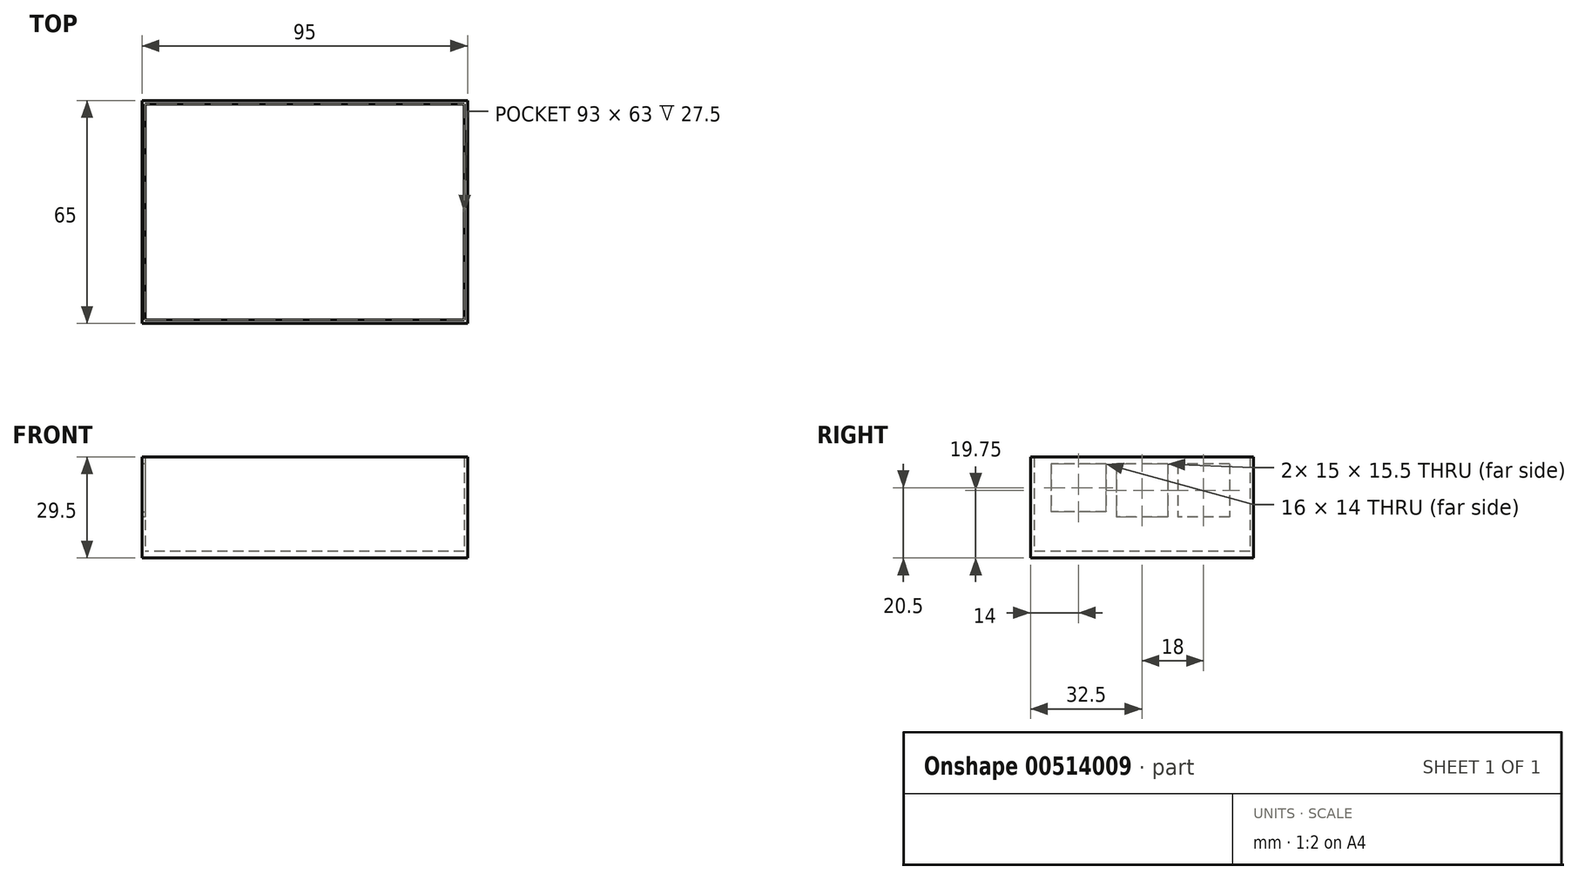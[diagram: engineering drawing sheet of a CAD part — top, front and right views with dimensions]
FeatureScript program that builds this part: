
annotation { "Feature Type Name" : "Feature", "Feature Type Description" : "" }
export const myFeature = defineFeature(function(context is Context, id is Id, definition is map)
    precondition{}
    {
        {
            var Q0;
            Q0=qCreatedBy(makeId("Top.planeOp"),FACE);
            var sketch = newSketch(context, id + "F0", { "sketchPlane" : qUnion([Q0])});
            skLineSegment(sketch, "E0.bottom", {"start": v(46.5, 31.5) * mm, "end": v(-46.5, 31.5) * mm});
            skLineSegment(sketch, "E0.top", {"start": v(46.5, -31.5) * mm, "end": v(-46.5, -31.5) * mm});
            skLineSegment(sketch, "E0.left", {"start": v(46.5, 31.5) * mm, "end": v(46.5, -31.5) * mm});
            skLineSegment(sketch, "E0.right", {"start": v(-46.5, 31.5) * mm, "end": v(-46.5, -31.5) * mm});
            skPoint(sketch, "E0.middle", {"position": v(0, 0) * mm});
            skLineSegment(sketch, "E1.bottom", {"start": v(47.5, 32.5) * mm, "end": v(-47.5, 32.5) * mm});
            skLineSegment(sketch, "E1.top", {"start": v(47.5, -32.5) * mm, "end": v(-47.5, -32.5) * mm});
            skLineSegment(sketch, "E1.left", {"start": v(47.5, 32.5) * mm, "end": v(47.5, -32.5) * mm});
            skLineSegment(sketch, "E1.right", {"start": v(-47.5, 32.5) * mm, "end": v(-47.5, -32.5) * mm});
            skSolve(sketch);
        }
        {
            var Q0;
            Q0=makeQuery(id+"F0.imprint","IMPRINT",FACE,{"disambiguationData":[TD([[makeQuery(id+"F0.imprint","IMPRINT",EDGE,{"derivedFrom":sQuery(id+"F0.wireOp",EDGE,"E0.bottom")}),-1.0]])]});
            extrude(context, id + "F1", {"entities" : qUnion([Q0]), "depth" : 12 * mm, "offsetDistance" : 25 * mm});
        }
        {
            var Q0;
            Q0=makeQuery(id+"F0.imprint","IMPRINT",FACE,{"disambiguationData":[TD([[makeQuery(id+"F0.imprint","IMPRINT",EDGE,{"derivedFrom":sQuery(id+"F0.wireOp",EDGE,"E0.bottom")}),1.0]])]});
            extrude(context, id + "F2", {"entities" : qUnion([Q0]), "operationType" : NewBodyOperationType.ADD, "depth" : 2 * mm, "offsetDistance" : 25 * mm});
        }
        {
            var Q0;
            Q0=makeQuery(id+"F1.opExtrude","CAP_FACE",FACE,{"disambiguationData":[OSD([sQuery(id+"F0.wireOp",EDGE,"E0.bottom"),sQuery(id+"F0.wireOp",EDGE,"E0.top"),sQuery(id+"F0.wireOp",EDGE,"E0.left"),sQuery(id+"F0.wireOp",EDGE,"E0.right"),sQuery(id+"F0.wireOp",EDGE,"E1.bottom"),sQuery(id+"F0.wireOp",EDGE,"E1.top"),sQuery(id+"F0.wireOp",EDGE,"E1.left"),sQuery(id+"F0.wireOp",EDGE,"E1.right")])],"isStart":false});
            var sketch = newSketch(context, id + "F3", { "sketchPlane" : qUnion([Q0])});
            skLineSegment(sketch, "E2.0", {"start": v(-47.5, 32.5) * mm, "end": v(-47.5, 25.5) * mm});
            skLineSegment(sketch, "E3.0", {"start": v(-46.5, 31.5) * mm, "end": v(-46.5, 25.5) * mm});
            skLineSegment(sketch, "E4.0", {"start": v(46.5, 31.5) * mm, "end": v(-46.5, 31.5) * mm});
            skLineSegment(sketch, "E5.0", {"start": v(47.5, 32.5) * mm, "end": v(-47.5, 32.5) * mm});
            skLineSegment(sketch, "E6.0", {"start": v(46.5, 31.5) * mm, "end": v(46.5, -31.5) * mm});
            skLineSegment(sketch, "E7.0", {"start": v(47.5, 32.5) * mm, "end": v(47.5, -32.5) * mm});
            skLineSegment(sketch, "E8.0", {"start": v(47.5, -32.5) * mm, "end": v(-47.5, -32.5) * mm});
            skLineSegment(sketch, "E9.0", {"start": v(46.5, -31.5) * mm, "end": v(-46.5, -31.5) * mm});
            skLineSegment(sketch, "E10", {"start": v(-46.5, 7.5) * mm, "end": v(-47.5, 7.5) * mm});
            skLineSegment(sketch, "E11", {"start": v(-46.5, -7.5) * mm, "end": v(-47.5, -7.5) * mm});
            skLineSegment(sketch, "E12", {"start": v(-46.5, 10.5) * mm, "end": v(-47.5, 10.5) * mm});
            skLineSegment(sketch, "E13", {"start": v(-47.5, 25.5) * mm, "end": v(-46.5, 25.5) * mm});
            skLineSegment(sketch, "E14.trimOffspring", {"start": v(-46.5, -7.5) * mm, "end": v(-46.5, -31.5) * mm});
            skLineSegment(sketch, "E15.trimOffspring", {"start": v(-47.5, -7.5) * mm, "end": v(-47.5, -32.5) * mm});
            skLineSegment(sketch, "E16.trimOffspring", {"start": v(-46.5, 10.5) * mm, "end": v(-46.5, 7.5) * mm});
            skLineSegment(sketch, "E17.trimOffspring", {"start": v(-47.5, 10.5) * mm, "end": v(-47.5, 7.5) * mm});
            skSolve(sketch);
        }
        {
            var Q0;
            Q0=makeQuery(id+"F3.imprint","IMPRINT",FACE,{"disambiguationData":[TD([[makeQuery(id+"F3.imprint","IMPRINT",EDGE,{"derivedFrom":sQuery(id+"F3.wireOp",EDGE,"E2.0")}),1.0]])]});
            var Q1;
            Q1=makeQuery(id+"F3.imprint","IMPRINT",FACE,{"disambiguationData":[TD([[makeQuery(id+"F3.imprint","IMPRINT",EDGE,{"derivedFrom":sQuery(id+"F3.wireOp",EDGE,"E10")}),-1.0]])]});
            extrude(context, id + "F4", {"entities" : qUnion([Q0, Q1]), "operationType" : NewBodyOperationType.ADD, "depth" : 1.5 * mm, "offsetDistance" : 25 * mm});
        }
        {
            var Q0;
            Q0=makeQuery(id+"F4.opExtrude","CAP_FACE",FACE,{"disambiguationData":[OSD([sQuery(id+"F3.wireOp",EDGE,"E2.0"),sQuery(id+"F3.wireOp",EDGE,"E3.0"),sQuery(id+"F3.wireOp",EDGE,"E4.0"),sQuery(id+"F3.wireOp",EDGE,"E5.0"),sQuery(id+"F3.wireOp",EDGE,"E6.0"),sQuery(id+"F3.wireOp",EDGE,"E7.0"),sQuery(id+"F3.wireOp",EDGE,"E8.0"),sQuery(id+"F3.wireOp",EDGE,"E9.0"),sQuery(id+"F3.wireOp",EDGE,"E11"),sQuery(id+"F3.wireOp",EDGE,"E13"),sQuery(id+"F3.wireOp",EDGE,"E14.trimOffspring"),sQuery(id+"F3.wireOp",EDGE,"E15.trimOffspring")])],"isStart":false});
            var sketch = newSketch(context, id + "F5", { "sketchPlane" : qUnion([Q0])});
            skLineSegment(sketch, "E18.0", {"start": v(47.5, 32.5) * mm, "end": v(-47.5, 32.5) * mm});
            skLineSegment(sketch, "E19.0", {"start": v(46.5, 31.5) * mm, "end": v(-46.5, 31.5) * mm});
            skLineSegment(sketch, "E20.0", {"start": v(-47.5, 32.5) * mm, "end": v(-47.5, 25.5) * mm});
            skLineSegment(sketch, "E21.0", {"start": v(-46.5, 31.5) * mm, "end": v(-46.5, 25.5) * mm});
            skLineSegment(sketch, "E22.0", {"start": v(-47.5, -7.5) * mm, "end": v(-47.5, -10.5) * mm});
            skLineSegment(sketch, "E23.0", {"start": v(-46.5, -7.5) * mm, "end": v(-46.5, -10.5) * mm});
            skLineSegment(sketch, "E24.0", {"start": v(47.5, -32.5) * mm, "end": v(-47.5, -32.5) * mm});
            skLineSegment(sketch, "E25.0", {"start": v(46.5, -31.5) * mm, "end": v(-46.5, -31.5) * mm});
            skLineSegment(sketch, "E26.0", {"start": v(46.5, 31.5) * mm, "end": v(46.5, -31.5) * mm});
            skLineSegment(sketch, "E27.0", {"start": v(47.5, 32.5) * mm, "end": v(47.5, -32.5) * mm});
            skPoint(sketch, "E28.0", {"position": v(-47, 25.5) * mm});
            skPoint(sketch, "E29.0", {"position": v(-47, 10.5) * mm});
            skLineSegment(sketch, "E30.0", {"start": v(-47.5, 10.5) * mm, "end": v(-47.5, 7.5) * mm});
            skLineSegment(sketch, "E31.0", {"start": v(-46.5, 10.5) * mm, "end": v(-46.5, 7.5) * mm});
            skLineSegment(sketch, "E32.0", {"start": v(-46.5, 10.5) * mm, "end": v(-47.5, 10.5) * mm});
            skLineSegment(sketch, "E33.0", {"start": v(-46.5, 7.5) * mm, "end": v(-47.5, 7.5) * mm});
            skLineSegment(sketch, "E34.0", {"start": v(-47.5, 25.5) * mm, "end": v(-46.5, 25.5) * mm});
            skLineSegment(sketch, "E35.0", {"start": v(-46.5, -7.5) * mm, "end": v(-47.5, -7.5) * mm});
            skLineSegment(sketch, "E36", {"start": v(-47.5, -10.5) * mm, "end": v(-46.5, -10.5) * mm});
            skLineSegment(sketch, "E37", {"start": v(-47.5, -26.5) * mm, "end": v(-46.5, -26.5) * mm});
            skLineSegment(sketch, "E38.trimOffspring", {"start": v(-46.5, -26.5) * mm, "end": v(-46.5, -31.5) * mm});
            skLineSegment(sketch, "E39.trimOffspring", {"start": v(-47.5, -26.5) * mm, "end": v(-47.5, -32.5) * mm});
            skSolve(sketch);
        }
        {
            var Q0;
            Q0=makeQuery(id+"F5.imprint","IMPRINT",FACE,{"disambiguationData":[TD([[makeQuery(id+"F5.imprint","IMPRINT",EDGE,{"derivedFrom":sQuery(id+"F5.wireOp",EDGE,"E18.0")}),1.0]])]});
            var Q1;
            Q1=makeQuery(id+"F5.imprint","IMPRINT",FACE,{"disambiguationData":[TD([[makeQuery(id+"F5.imprint","IMPRINT",EDGE,{"derivedFrom":sQuery(id+"F5.wireOp",EDGE,"E22.0")}),1.0]])]});
            var Q2;
            Q2=makeQuery(id+"F5.imprint","IMPRINT",FACE,{"disambiguationData":[TD([[makeQuery(id+"F5.imprint","IMPRINT",EDGE,{"derivedFrom":sQuery(id+"F5.wireOp",EDGE,"E30.0")}),1.0]])]});
            extrude(context, id + "F6", {"entities" : qUnion([Q0, Q1, Q2]), "operationType" : NewBodyOperationType.ADD, "depth" : 14 * mm, "offsetDistance" : 25 * mm});
        }
        {
            var Q0;
            Q0=makeQuery(id+"F6.opExtrude","CAP_FACE",FACE,{"disambiguationData":[OSD([sQuery(id+"F5.wireOp",EDGE,"E18.0"),sQuery(id+"F5.wireOp",EDGE,"E19.0"),sQuery(id+"F5.wireOp",EDGE,"E20.0"),sQuery(id+"F5.wireOp",EDGE,"E21.0"),sQuery(id+"F5.wireOp",EDGE,"E24.0"),sQuery(id+"F5.wireOp",EDGE,"E25.0"),sQuery(id+"F5.wireOp",EDGE,"E26.0"),sQuery(id+"F5.wireOp",EDGE,"E27.0"),sQuery(id+"F5.wireOp",EDGE,"E34.0"),sQuery(id+"F5.wireOp",EDGE,"E37"),sQuery(id+"F5.wireOp",EDGE,"E38.trimOffspring"),sQuery(id+"F5.wireOp",EDGE,"E39.trimOffspring")])],"isStart":false});
            var sketch = newSketch(context, id + "F7", { "sketchPlane" : qUnion([Q0])});
            skLineSegment(sketch, "E40.0", {"start": v(47.5, 32.5) * mm, "end": v(-47.5, 32.5) * mm});
            skLineSegment(sketch, "E41.0", {"start": v(46.5, 31.5) * mm, "end": v(-46.5, 31.5) * mm});
            skLineSegment(sketch, "E42.0", {"start": v(46.5, 31.5) * mm, "end": v(46.5, -31.5) * mm});
            skLineSegment(sketch, "E43.0", {"start": v(46.5, -31.5) * mm, "end": v(-46.5, -31.5) * mm});
            skLineSegment(sketch, "E44.0", {"start": v(47.5, 32.5) * mm, "end": v(47.5, -32.5) * mm});
            skLineSegment(sketch, "E45.0", {"start": v(47.5, -32.5) * mm, "end": v(-47.5, -32.5) * mm});
            skLineSegment(sketch, "E46", {"start": v(-46.5, 31.5) * mm, "end": v(-46.5, -31.5) * mm});
            skLineSegment(sketch, "E47", {"start": v(-47.5, 32.5) * mm, "end": v(-47.5, -32.5) * mm});
            skSolve(sketch);
        }
        {
            var Q0;
            Q0 = qSketchRegion(id + "F7", true);
            extrude(context, id + "F8", {"entities" : qUnion([Q0]), "operationType" : NewBodyOperationType.ADD, "depth" : 2 * mm, "offsetDistance" : 25 * mm});
        }
    });
